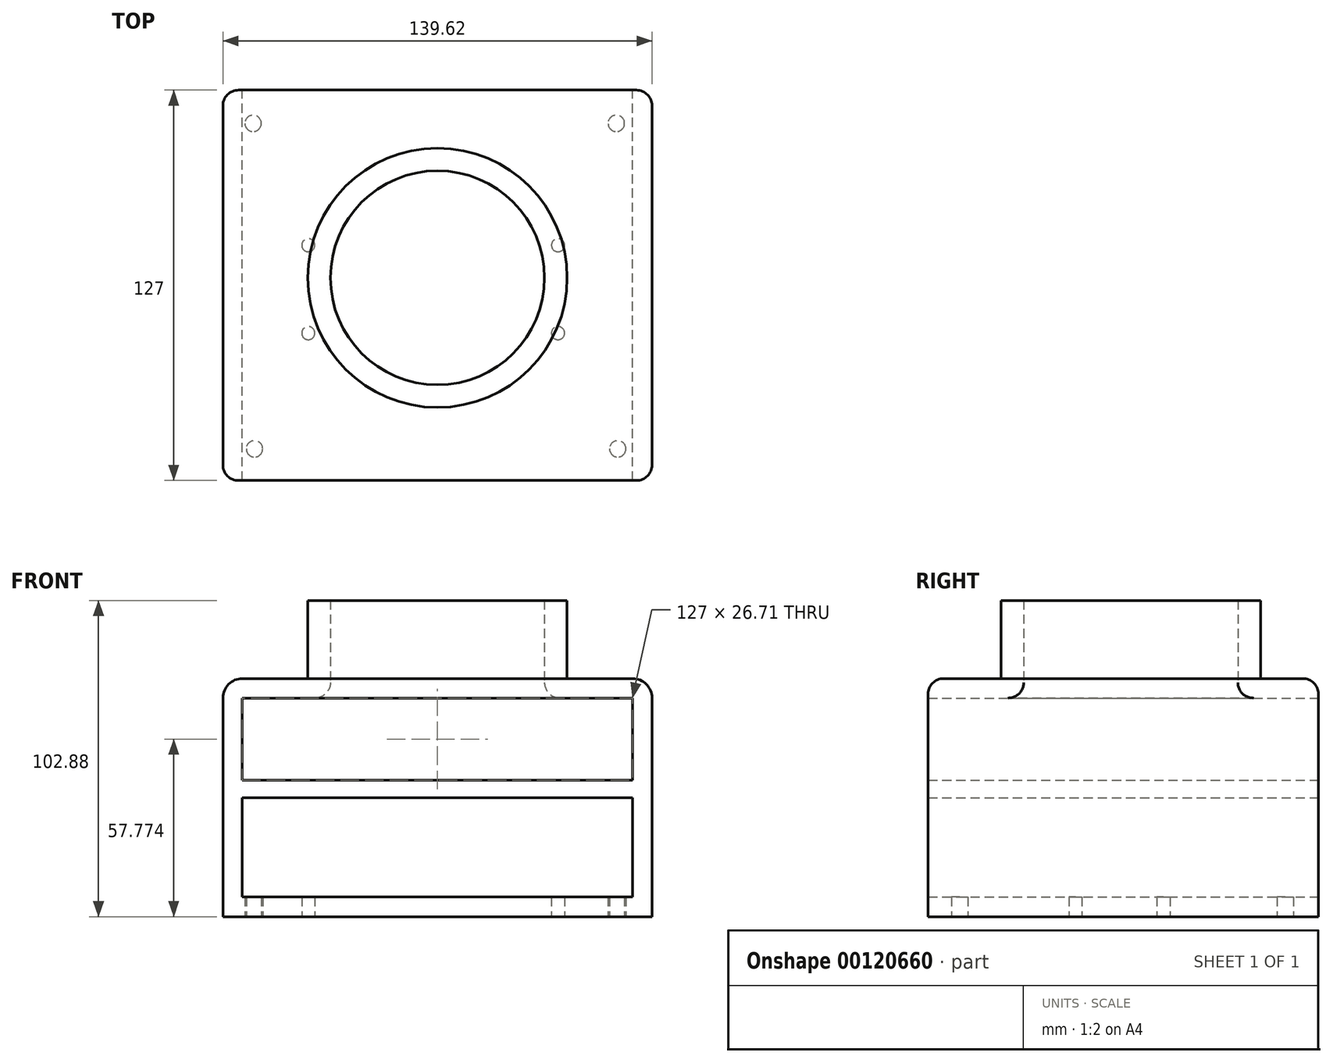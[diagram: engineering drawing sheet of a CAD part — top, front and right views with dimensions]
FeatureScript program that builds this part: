
annotation { "Feature Type Name" : "Feature", "Feature Type Description" : "" }
export const myFeature = defineFeature(function(context is Context, id is Id, definition is map)
    precondition{}
    {
        {
            var Q0;
            Q0=qCreatedBy(makeId("Front.planeOp"),FACE);
            var sketch = newSketch(context, id + "F0", { "sketchPlane" : qUnion([Q0])});
            skLineSegment(sketch, "E0.bottom", {"start": v(63.46, 38.74) * mm, "end": v(-63.46, 38.74) * mm});
            skLineSegment(sketch, "E0.top", {"start": v(69.8, -38.74) * mm, "end": v(-69.8, -38.74) * mm});
            skLineSegment(sketch, "E0.left", {"start": v(69.8, 32.4) * mm, "end": v(69.8, -38.74) * mm});
            skLineSegment(sketch, "E0.right", {"start": v(-69.8, 32.4) * mm, "end": v(-69.8, -38.74) * mm});
            skPoint(sketch, "E0.middle", {"position": v(0, 0) * mm});
            skPoint(sketch, "E1.visualSharp", {"position": v(-69.8, 38.74) * mm});
            skArc(sketch, "E1.filletArc", {"start": v(-63.46, 38.74) * mm, "mid": v(-67.95, 36.88) * mm, "end": v(-69.8, 32.4) * mm});
            skPoint(sketch, "E2.visualSharp", {"position": v(69.8, 38.74) * mm});
            skArc(sketch, "E2.filletArc", {"start": v(69.8, 32.4) * mm, "mid": v(67.95, 36.88) * mm, "end": v(63.46, 38.74) * mm});
            skLineSegment(sketch, "E3.bottom", {"start": v(-63.54, -32.36) * mm, "end": v(63.46, -32.36) * mm});
            skLineSegment(sketch, "E3.top", {"start": v(-63.54, 0) * mm, "end": v(63.46, 0) * mm});
            skLineSegment(sketch, "E3.left", {"start": v(-63.54, -32.36) * mm, "end": v(-63.54, 0) * mm});
            skLineSegment(sketch, "E3.right", {"start": v(63.46, -32.36) * mm, "end": v(63.46, 0) * mm});
            skLineSegment(sketch, "E4.bottom", {"start": v(-63.54, 5.68) * mm, "end": v(63.46, 5.68) * mm});
            skLineSegment(sketch, "E4.top", {"start": v(-63.54, 32.4) * mm, "end": v(63.46, 32.4) * mm});
            skLineSegment(sketch, "E4.left", {"start": v(-63.54, 5.68) * mm, "end": v(-63.54, 32.4) * mm});
            skLineSegment(sketch, "E4.right", {"start": v(63.46, 5.68) * mm, "end": v(63.46, 32.4) * mm});
            skSolve(sketch);
        }
        {
            var Q0;
            Q0=makeQuery(id+"F0.imprint","IMPRINT",FACE,{"disambiguationData":[TD([[makeQuery(id+"F0.imprint","IMPRINT",EDGE,{"derivedFrom":sQuery(id+"F0.wireOp",EDGE,"E0.bottom")}),1.0]])]});
            extrude(context, id + "F1", {"entities" : qUnion([Q0]), "offsetDistance" : 25.4 * mm, "depth" : 127 * mm});
        }
        {
            var Q0;
            Q0=makeQuery(id+"F1.opExtrude","CAP_EDGE",EDGE,{"disambiguationData":[OSD([sQuery(id+"F0.wireOp",EDGE,"E0.left")])],"isStart":false});
            var Q1;
            Q1=makeQuery(id+"F1.opExtrude","CAP_EDGE",EDGE,{"disambiguationData":[OSD([sQuery(id+"F0.wireOp",EDGE,"E2.filletArc")])],"isStart":false});
            var Q2;
            Q2=makeQuery(id+"F1.opExtrude","CAP_EDGE",EDGE,{"disambiguationData":[OSD([sQuery(id+"F0.wireOp",EDGE,"E0.bottom")])],"isStart":false});
            var Q3;
            Q3=makeQuery(id+"F1.opExtrude","CAP_EDGE",EDGE,{"disambiguationData":[OSD([sQuery(id+"F0.wireOp",EDGE,"E1.filletArc")])],"isStart":false});
            var Q4;
            Q4=makeQuery(id+"F1.opExtrude","CAP_EDGE",EDGE,{"disambiguationData":[OSD([sQuery(id+"F0.wireOp",EDGE,"E0.right")])],"isStart":false});
            var Q5;
            Q5=makeQuery(id+"F1.opExtrude","CAP_EDGE",EDGE,{"disambiguationData":[OSD([sQuery(id+"F0.wireOp",EDGE,"E0.left")])],"isStart":true});
            var Q6;
            Q6=makeQuery(id+"F1.opExtrude","CAP_EDGE",EDGE,{"disambiguationData":[OSD([sQuery(id+"F0.wireOp",EDGE,"E2.filletArc")])],"isStart":true});
            var Q7;
            Q7=makeQuery(id+"F1.opExtrude","CAP_EDGE",EDGE,{"disambiguationData":[OSD([sQuery(id+"F0.wireOp",EDGE,"E0.bottom")])],"isStart":true});
            var Q8;
            Q8=makeQuery(id+"F1.opExtrude","CAP_EDGE",EDGE,{"disambiguationData":[OSD([sQuery(id+"F0.wireOp",EDGE,"E1.filletArc")])],"isStart":true});
            var Q9;
            Q9=makeQuery(id+"F1.opExtrude","CAP_EDGE",EDGE,{"disambiguationData":[OSD([sQuery(id+"F0.wireOp",EDGE,"E0.right")])],"isStart":true});
            fillet(context, id + "F2", {"entities" : qUnion([Q0, Q1, Q2, Q3, Q4, Q5, Q6, Q7, Q8, Q9]), "radius" : 5.08 * mm, "tangentPropagation" : true, "allowEdgeOverflow" : false});
        }
        {
            var Q0;
            Q0=makeQuery(id+"F1.opExtrude","SWEPT_FACE",FACE,{"disambiguationData":[OSD([sQuery(id+"F0.wireOp",EDGE,"E0.top")])]});
            var sketch = newSketch(context, id + "F3", { "sketchPlane" : qUnion([Q0])});
            skCircle(sketch, "E5", {"center": v(-42.02, 79.05) * mm, "radius": 2.13 * mm});
            skCircle(sketch, "E6.0.1.0", {"center": v(-42.02, 50.46) * mm, "radius": 2.13 * mm});
            skCircle(sketch, "E6.1.0.0", {"center": v(39.22, 79.05) * mm, "radius": 2.13 * mm});
            skCircle(sketch, "E6.1.1.0", {"center": v(39.22, 50.46) * mm, "radius": 2.13 * mm});
            skLineSegment(sketch, "E6.direction1", {"start": v(-42.02, 79.05) * mm, "end": v(39.22, 79.05) * mm, "construction": true});
            skLineSegment(sketch, "E6.direction2", {"start": v(-42.02, 79.05) * mm, "end": v(-42.02, 50.46) * mm, "construction": true});
            skSolve(sketch);
        }
        {
            var Q0;
            Q0 = qSketchRegion(id + "F3", true);
            extrude(context, id + "F4", {"entities" : qUnion([Q0]), "operationType" : NewBodyOperationType.REMOVE, "oppositeDirection" : true, "offsetDistance" : 25.4 * mm, "depth" : 25.4 * mm});
        }
        {
            var Q0;
            Q0=makeQuery(id+"F1.opExtrude","SWEPT_FACE",FACE,{"disambiguationData":[OSD([sQuery(id+"F0.wireOp",EDGE,"E0.top")])]});
            var sketch = newSketch(context, id + "F5", { "sketchPlane" : qUnion([Q0])});
            skCircle(sketch, "E7", {"center": v(-59.53, 116.69) * mm, "radius": 2.67 * mm});
            skCircle(sketch, "E8.0.1.0", {"center": v(-59.99, 10.82) * mm, "radius": 2.67 * mm});
            skCircle(sketch, "E8.1.0.0", {"center": v(58.64, 116.69) * mm, "radius": 2.67 * mm});
            skCircle(sketch, "E8.1.1.0", {"center": v(58.19, 10.82) * mm, "radius": 2.67 * mm});
            skLineSegment(sketch, "E8.direction1", {"start": v(-59.53, 116.69) * mm, "end": v(58.64, 116.69) * mm, "construction": true});
            skLineSegment(sketch, "E8.direction2", {"start": v(-59.53, 116.69) * mm, "end": v(-59.99, 10.82) * mm, "construction": true});
            skSolve(sketch);
        }
        {
            var Q0;
            Q0 = qSketchRegion(id + "F5", true);
            extrude(context, id + "F6", {"entities" : qUnion([Q0]), "operationType" : NewBodyOperationType.REMOVE, "oppositeDirection" : true, "offsetDistance" : 25.4 * mm, "depth" : 25.4 * mm});
        }
        {
            var Q0;
            Q0=makeQuery(id+"F1.opExtrude","SWEPT_FACE",FACE,{"disambiguationData":[OSD([sQuery(id+"F0.wireOp",EDGE,"E0.bottom")])]});
            var sketch = newSketch(context, id + "F7", { "sketchPlane" : qUnion([Q0])});
            skCircle(sketch, "E9", {"center": v(0, -61.05) * mm, "radius": 42.18 * mm});
            skCircle(sketch, "E10", {"center": v(0, -61.05) * mm, "radius": 34.81 * mm});
            skSolve(sketch);
        }
        {
            var Q0;
            Q0 = qSketchRegion(id + "F7", true);
            extrude(context, id + "F8", {"entities" : qUnion([Q0]), "operationType" : NewBodyOperationType.ADD, "depth" : 25.4 * mm});
        }
        {
            var Q0;
            Q0=makeQuery(id+"F8.boolean.opBoolean","SPLIT",FACE,{"disambiguationData":[TD([makeQuery(id+"F8.opExtrude","SWEPT_FACE",FACE,{"disambiguationData":[OSD([sQuery(id+"F7.wireOp",EDGE,"E10")])]})])],"derivedFrom":makeQuery(id+"F1.opExtrude","SWEPT_FACE",FACE,{"disambiguationData":[OSD([sQuery(id+"F0.wireOp",EDGE,"E0.bottom")])]})});
            extrude(context, id + "F9", {"entities" : qUnion([Q0]), "operationType" : NewBodyOperationType.REMOVE, "oppositeDirection" : true, "depth" : 25.4 * mm});
        }
        {
            var Q0;
            Q0=makeQuery(id+"F9.boolean.opBoolean","INTERSECT",EDGE,{"derivedFrom":[makeQuery(id+"F1.opExtrude","SWEPT_FACE",FACE,{"disambiguationData":[OSD([sQuery(id+"F0.wireOp",EDGE,"E4.top")])]}),makeQuery(id+"F9.opExtrude","SWEPT_FACE",FACE,{"disambiguationData":[OSD([sQuery(id+"F7.wireOp",EDGE,"E10")])]})]});
            fillet(context, id + "F10", {"entities" : qUnion([Q0]), "radius" : 5.08 * mm, "tangentPropagation" : true, "allowEdgeOverflow" : false});
        }
    });
